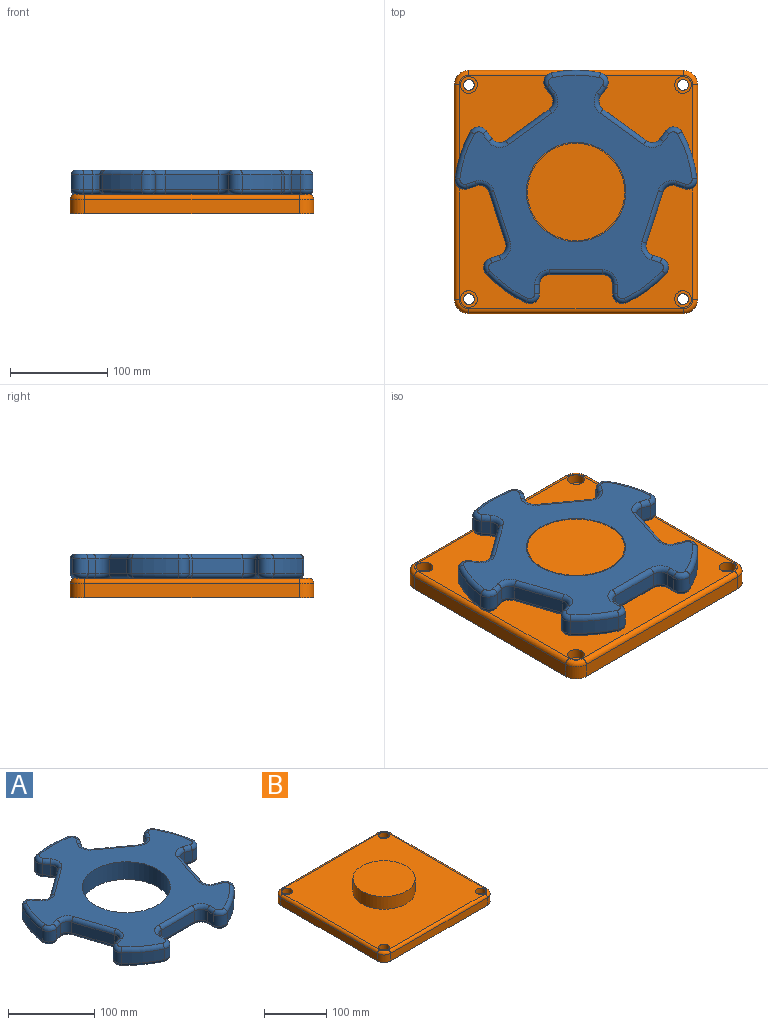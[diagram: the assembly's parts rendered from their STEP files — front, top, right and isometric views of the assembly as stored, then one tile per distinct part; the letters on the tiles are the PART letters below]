
ASSEMBLY  parts=2 mates=1
PART A: 123 faces, bbox 268.9x258.5x25 mm
  f0: plane 238.57x229.73mm, normal (0,0,1), area 21505.7mm2, adj f6,f43,f44,f45,f46,f47,f48,f49
  f1: plane 238.57x229.73mm, normal (0,0,-1), area 21505.7mm2, adj f6,f83,f84,f85,f86,f87,f88,f89
  f2: cylinder r=125mm len=40.68mm, axis (0,0,-1), area 759.5mm2, adj f13,f42,f51,f91
  f3: cylinder r=125mm len=47.82mm, axis (0,0,-1), area 759.5mm2, adj f35,f41,f67,f107
  f4: cylinder r=125mm len=50.29mm, axis (0,0,-1), area 759.5mm2, adj f28,f34,f82,f122
  f5: cylinder r=125mm len=47.82mm, axis (0,0,-1), area 759.5mm2, adj f21,f27,f66,f106
  f6: cylinder r=51mm len=102mm, axis (0,0,-1), area 8011.1mm2, adj f0,f1
  f7: cylinder r=125mm len=40.68mm, axis (0,0,-1), area 759.5mm2, adj f14,f20,f50,f90
  f8: plane 15x9.73mm, normal (-1,0,0), area 146mm2, adj f11,f14,f46,f86
  f9: plane 55x15mm, normal (0,-1,0), area 825mm2, adj f11,f12,f43,f83
  f10: plane 15x9.73mm, normal (1,0,0), area 146mm2, adj f12,f13,f47,f87
  f11: cylinder r=10mm len=15mm, axis (0,0,-1), area 235.6mm2, adj f8,f9,f44,f84
  f12: cylinder r=10mm len=15mm, axis (0,0,-1), area 235.6mm2, adj f9,f10,f45,f85
  f13: cylinder r=10mm len=15mm, axis (0,0,-1), area 299.5mm2, adj f2,f10,f49,f89
  f14: cylinder r=10mm len=15mm, axis (0,0,-1), area 299.5mm2, adj f7,f8,f48,f88
  f15: plane 15x9.26mm, normal (-0.31,-0.95,0), area 146mm2, adj f18,f21,f62,f102
  f16: plane 52.31x17mm, normal (0.95,-0.31,0), area 825mm2, adj f18,f19,f58,f98
  f17: plane 15x9.26mm, normal (0.31,0.95,0), area 146mm2, adj f19,f20,f54,f94
  f18: cylinder r=10mm len=15mm, axis (0,0,-1), area 235.6mm2, adj f15,f16,f60,f100
  f19: cylinder r=10mm len=15mm, axis (0,0,-1), area 235.6mm2, adj f16,f17,f56,f96
  f20: cylinder r=10mm len=16.25mm, axis (0,0,-1), area 299.5mm2, adj f7,f17,f52,f92
  f21: cylinder r=10mm len=15mm, axis (0,0,-1), area 299.5mm2, adj f5,f15,f64,f104
  f22: plane 15x7.87mm, normal (0.81,-0.59,0), area 146mm2, adj f25,f28,f78,f118
  f23: plane 44.5x32.33mm, normal (0.59,0.81,0), area 825mm2, adj f25,f26,f74,f114
  f24: plane 15x7.87mm, normal (-0.81,0.59,0), area 146mm2, adj f26,f27,f70,f110
  f25: cylinder r=10mm len=15mm, axis (0,0,-1), area 235.6mm2, adj f22,f23,f76,f116
  f26: cylinder r=10mm len=15mm, axis (0,0,-1), area 235.6mm2, adj f23,f24,f72,f112
  f27: cylinder r=10mm len=16.78mm, axis (0,0,-1), area 299.5mm2, adj f5,f24,f68,f108
  f28: cylinder r=10mm len=15.67mm, axis (0,0,-1), area 299.5mm2, adj f4,f22,f80,f120
  f29: plane 15x7.87mm, normal (0.81,0.59,0), area 146mm2, adj f32,f35,f71,f111
  f30: plane 44.5x32.33mm, normal (-0.59,0.81,0), area 825mm2, adj f32,f33,f75,f115
  f31: plane 15x7.87mm, normal (-0.81,-0.59,0), area 146mm2, adj f33,f34,f79,f119
  f32: cylinder r=10mm len=15mm, axis (0,0,-1), area 235.6mm2, adj f29,f30,f73,f113
  f33: cylinder r=10mm len=15mm, axis (0,0,-1), area 235.6mm2, adj f30,f31,f77,f117
  f34: cylinder r=10mm len=15.67mm, axis (0,0,-1), area 299.5mm2, adj f4,f31,f81,f121
  f35: cylinder r=10mm len=16.78mm, axis (0,0,-1), area 299.5mm2, adj f3,f29,f69,f109
  f36: plane 15x9.26mm, normal (-0.31,0.95,0), area 146mm2, adj f39,f42,f55,f95
  f37: plane 52.31x17mm, normal (-0.95,-0.31,0), area 825mm2, adj f39,f40,f59,f99
  f38: plane 15x9.26mm, normal (0.31,-0.95,0), area 146mm2, adj f40,f41,f63,f103
  f39: cylinder r=10mm len=15mm, axis (0,0,-1), area 235.6mm2, adj f36,f37,f57,f97
  f40: cylinder r=10mm len=15mm, axis (0,0,-1), area 235.6mm2, adj f37,f38,f61,f101
  f41: cylinder r=10mm len=15mm, axis (0,0,-1), area 299.5mm2, adj f3,f38,f65,f105
  f42: cylinder r=10mm len=16.25mm, axis (0,0,-1), area 299.5mm2, adj f2,f36,f53,f93
  f43: cylinder r=5mm len=55mm, axis (1,0,0), area 432mm2, adj f0,f9,f44,f45
  f44: torus R=15mm, axis (0,0,1), area 145.8mm2, adj f0,f11,f43,f46
  f45: torus R=15mm, axis (0,0,1), area 145.8mm2, adj f0,f12,f43,f47
  f46: cylinder r=5mm len=9.73mm, axis (0,-1,0), area 76.4mm2, adj f0,f8,f44,f48
  f47: cylinder r=5mm len=9.73mm, axis (0,1,0), area 76.4mm2, adj f0,f10,f45,f49
  f48: torus R=5mm, axis (0,0,1), area 128.3mm2, adj f0,f14,f46,f50
  f49: torus R=5mm, axis (0,0,1), area 128.3mm2, adj f0,f13,f47,f51
  f50: torus R=120mm, axis (0,0,1), area 391.9mm2, adj f0,f7,f48,f52
  f51: torus R=120mm, axis (0,0,1), area 391.9mm2, adj f0,f2,f49,f53
  f52: torus R=5mm, axis (0,0,1), area 128.3mm2, adj f0,f20,f50,f54
  f53: torus R=5mm, axis (0,0,1), area 128.3mm2, adj f0,f42,f51,f55
  f54: cylinder r=5mm len=10.8mm, axis (-0.95,0.31,0), area 76.4mm2, adj f0,f17,f52,f56
  f55: cylinder r=5mm len=10.8mm, axis (-0.95,-0.31,0), area 76.4mm2, adj f0,f36,f53,f57
  f56: torus R=15mm, axis (0,0,1), area 145.8mm2, adj f0,f19,f54,f58
  f57: torus R=15mm, axis (0,0,1), area 145.8mm2, adj f0,f39,f55,f59
  f58: cylinder r=5mm len=53.85mm, axis (0.31,0.95,0), area 432mm2, adj f0,f16,f56,f60
  f59: cylinder r=5mm len=53.85mm, axis (0.31,-0.95,0), area 432mm2, adj f0,f37,f57,f61
  f60: torus R=15mm, axis (0,0,1), area 145.8mm2, adj f0,f18,f58,f62
  f61: torus R=15mm, axis (0,0,1), area 145.8mm2, adj f0,f40,f59,f63
  f62: cylinder r=5mm len=10.8mm, axis (0.95,-0.31,0), area 76.4mm2, adj f0,f15,f60,f64
  f63: cylinder r=5mm len=10.8mm, axis (0.95,0.31,0), area 76.4mm2, adj f0,f38,f61,f65
  f64: torus R=5mm, axis (0,0,1), area 128.3mm2, adj f0,f21,f62,f66
  f65: torus R=5mm, axis (0,0,1), area 128.3mm2, adj f0,f41,f63,f67
  f66: torus R=120mm, axis (0,0,1), area 391.9mm2, adj f0,f5,f64,f68
  f67: torus R=120mm, axis (0,0,1), area 391.9mm2, adj f0,f3,f65,f69
  f68: torus R=5mm, axis (0,0,1), area 128.3mm2, adj f0,f27,f66,f70
  f69: torus R=5mm, axis (0,0,1), area 128.3mm2, adj f0,f35,f67,f71
  f70: cylinder r=5mm len=10.81mm, axis (-0.59,-0.81,0), area 76.4mm2, adj f0,f24,f68,f72
  f71: cylinder r=5mm len=10.81mm, axis (-0.59,0.81,0), area 76.4mm2, adj f0,f29,f69,f73
  f72: torus R=15mm, axis (0,0,1), area 145.8mm2, adj f0,f26,f70,f74
  f73: torus R=15mm, axis (0,0,1), area 145.8mm2, adj f0,f32,f71,f75
  f74: cylinder r=5mm len=47.44mm, axis (-0.81,0.59,0), area 432mm2, adj f0,f23,f72,f76
  f75: cylinder r=5mm len=47.44mm, axis (-0.81,-0.59,0), area 432mm2, adj f0,f30,f73,f77
  f76: torus R=15mm, axis (0,0,1), area 145.8mm2, adj f0,f25,f74,f78
  f77: torus R=15mm, axis (0,0,1), area 145.8mm2, adj f0,f33,f75,f79
  f78: cylinder r=5mm len=10.81mm, axis (0.59,0.81,0), area 76.4mm2, adj f0,f22,f76,f80
  f79: cylinder r=5mm len=10.81mm, axis (0.59,-0.81,0), area 76.4mm2, adj f0,f31,f77,f81
  f80: torus R=5mm, axis (0,0,1), area 128.3mm2, adj f0,f28,f78,f82
  f81: torus R=5mm, axis (0,0,1), area 128.3mm2, adj f0,f34,f79,f82
  f82: torus R=120mm, axis (0,0,1), area 391.9mm2, adj f0,f4,f80,f81
  f83: cylinder r=5mm len=55mm, axis (-1,0,0), area 432mm2, adj f1,f9,f84,f85
  f84: torus R=15mm, axis (0,0,1), area 145.8mm2, adj f1,f11,f83,f86
  f85: torus R=15mm, axis (0,0,1), area 145.8mm2, adj f1,f12,f83,f87
  f86: cylinder r=5mm len=9.73mm, axis (0,1,0), area 76.4mm2, adj f1,f8,f84,f88
  f87: cylinder r=5mm len=9.73mm, axis (0,-1,0), area 76.4mm2, adj f1,f10,f85,f89
  f88: torus R=5mm, axis (0,0,1), area 128.3mm2, adj f1,f14,f86,f90
  f89: torus R=5mm, axis (0,0,1), area 128.3mm2, adj f1,f13,f87,f91
  f90: torus R=120mm, axis (0,0,1), area 391.9mm2, adj f1,f7,f88,f92
  f91: torus R=120mm, axis (0,0,1), area 391.9mm2, adj f1,f2,f89,f93
  f92: torus R=5mm, axis (0,0,1), area 128.3mm2, adj f1,f20,f90,f94
  f93: torus R=5mm, axis (0,0,1), area 128.3mm2, adj f1,f42,f91,f95
  f94: cylinder r=5mm len=10.8mm, axis (0.95,-0.31,0), area 76.4mm2, adj f1,f17,f92,f96
  f95: cylinder r=5mm len=10.8mm, axis (0.95,0.31,0), area 76.4mm2, adj f1,f36,f93,f97
  f96: torus R=15mm, axis (0,0,1), area 145.8mm2, adj f1,f19,f94,f98
  f97: torus R=15mm, axis (0,0,1), area 145.8mm2, adj f1,f39,f95,f99
  f98: cylinder r=5mm len=53.85mm, axis (-0.31,-0.95,0), area 432mm2, adj f1,f16,f96,f100
  f99: cylinder r=5mm len=53.85mm, axis (-0.31,0.95,0), area 432mm2, adj f1,f37,f97,f101
  f100: torus R=15mm, axis (0,0,1), area 145.8mm2, adj f1,f18,f98,f102
  f101: torus R=15mm, axis (0,0,1), area 145.8mm2, adj f1,f40,f99,f103
  f102: cylinder r=5mm len=10.8mm, axis (-0.95,0.31,0), area 76.4mm2, adj f1,f15,f100,f104
  f103: cylinder r=5mm len=10.8mm, axis (-0.95,-0.31,0), area 76.4mm2, adj f1,f38,f101,f105
  f104: torus R=5mm, axis (0,0,1), area 128.3mm2, adj f1,f21,f102,f106
  f105: torus R=5mm, axis (0,0,1), area 128.3mm2, adj f1,f41,f103,f107
  f106: torus R=120mm, axis (0,0,1), area 391.9mm2, adj f1,f5,f104,f108
  f107: torus R=120mm, axis (0,0,1), area 391.9mm2, adj f1,f3,f105,f109
  f108: torus R=5mm, axis (0,0,1), area 128.3mm2, adj f1,f27,f106,f110
  f109: torus R=5mm, axis (0,0,1), area 128.3mm2, adj f1,f35,f107,f111
  f110: cylinder r=5mm len=10.81mm, axis (0.59,0.81,0), area 76.4mm2, adj f1,f24,f108,f112
  f111: cylinder r=5mm len=10.81mm, axis (0.59,-0.81,0), area 76.4mm2, adj f1,f29,f109,f113
  f112: torus R=15mm, axis (0,0,1), area 145.8mm2, adj f1,f26,f110,f114
  f113: torus R=15mm, axis (0,0,1), area 145.8mm2, adj f1,f32,f111,f115
  f114: cylinder r=5mm len=47.44mm, axis (0.81,-0.59,0), area 432mm2, adj f1,f23,f112,f116
  f115: cylinder r=5mm len=47.44mm, axis (0.81,0.59,0), area 432mm2, adj f1,f30,f113,f117
  f116: torus R=15mm, axis (0,0,1), area 145.8mm2, adj f1,f25,f114,f118
  f117: torus R=15mm, axis (0,0,1), area 145.8mm2, adj f1,f33,f115,f119
  f118: cylinder r=5mm len=10.81mm, axis (-0.59,-0.81,0), area 76.4mm2, adj f1,f22,f116,f120
  f119: cylinder r=5mm len=10.81mm, axis (-0.59,0.81,0), area 76.4mm2, adj f1,f31,f117,f121
  f120: torus R=5mm, axis (0,0,1), area 128.3mm2, adj f1,f28,f118,f122
  f121: torus R=5mm, axis (0,0,1), area 128.3mm2, adj f1,f34,f119,f122
  f122: torus R=120mm, axis (0,0,1), area 391.9mm2, adj f1,f4,f120,f121
PART B: 32 faces, bbox 252.5x252.5x45 mm
  f0: plane 220x15mm, normal (1,0,0), area 3300mm2, adj f5,f8,f11,f27
  f1: plane 220x15mm, normal (0,1,0), area 3300mm2, adj f5,f8,f9,f31
  f2: plane 220x15mm, normal (-1,0,0), area 3300mm2, adj f5,f9,f10,f28
  f3: plane 220x15mm, normal (0,-1,0), area 3300mm2, adj f5,f10,f11,f24
  f4: plane 240x240mm, normal (0,0,1), area 48725.4mm2, adj f6,f14,f17,f20,f23,f24,f25,f26
  f5: plane 250x250mm, normal (0,0,-1), area 61926.7mm2, adj f0,f1,f2,f3,f8,f9,f10,f11
  f6: cylinder r=50mm len=100mm, axis (0,0,-1), area 7854mm2, adj f4,f7
  f7: plane 100x100mm, normal (0,0,1), area 7854mm2, adj f6
  f8: cylinder r=15mm len=15mm, axis (0,0,-1), area 353.4mm2, adj f0,f1,f5,f29
  f9: cylinder r=15mm len=15mm, axis (0,0,1), area 353.4mm2, adj f1,f2,f5,f30
  f10: cylinder r=15mm len=15mm, axis (0,0,-1), area 353.4mm2, adj f2,f3,f5,f26
  f11: cylinder r=15mm len=15mm, axis (0,0,1), area 353.4mm2, adj f0,f3,f5,f25
  f12: cylinder r=5.5mm len=11mm, axis (0,0,1), area 345.6mm2, adj f5,f13
  f13: plane 17.25x17.25mm, normal (0,0,1), area 138.7mm2, adj f12,f14
  f14: cylinder r=8.62mm len=17.25mm, axis (0,0,1), area 541.9mm2, adj f4,f13
  f15: cylinder r=5.5mm len=11mm, axis (0,0,1), area 345.6mm2, adj f5,f16
  f16: plane 17.25x17.25mm, normal (0,0,1), area 138.7mm2, adj f15,f17
  f17: cylinder r=8.62mm len=17.25mm, axis (0,0,1), area 541.9mm2, adj f4,f16
  f18: cylinder r=5.5mm len=11mm, axis (0,0,1), area 345.6mm2, adj f5,f19
  f19: plane 17.25x17.25mm, normal (0,0,1), area 138.7mm2, adj f18,f20
  f20: cylinder r=8.62mm len=17.25mm, axis (0,0,1), area 541.9mm2, adj f4,f19
  f21: cylinder r=5.5mm len=11mm, axis (0,0,1), area 345.6mm2, adj f5,f22
  f22: plane 17.25x17.25mm, normal (0,0,1), area 138.7mm2, adj f21,f23
  f23: cylinder r=8.62mm len=17.25mm, axis (0,0,1), area 541.9mm2, adj f4,f22
  f24: cylinder r=5mm len=220mm, axis (-1,0,0), area 1727.9mm2, adj f3,f4,f25,f26
  f25: torus R=10mm, axis (0,0,1), area 162.6mm2, adj f4,f11,f24,f27
  f26: torus R=10mm, axis (0,0,1), area 162.6mm2, adj f4,f10,f24,f28
  f27: cylinder r=5mm len=220mm, axis (0,-1,0), area 1727.9mm2, adj f0,f4,f25,f29
  f28: cylinder r=5mm len=220mm, axis (0,1,0), area 1727.9mm2, adj f2,f4,f26,f30
  f29: torus R=10mm, axis (0,0,1), area 162.6mm2, adj f4,f8,f27,f31
  f30: torus R=10mm, axis (0,0,1), area 162.6mm2, adj f4,f9,f28,f31
  f31: cylinder r=5mm len=220mm, axis (1,0,0), area 1727.9mm2, adj f1,f4,f29,f30
PLACE A at identity
PLACE B at identity fixed
MATE revolute B.f6 <-> A.f2  axis (0,0,1) through (0,0,20)mm
